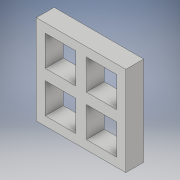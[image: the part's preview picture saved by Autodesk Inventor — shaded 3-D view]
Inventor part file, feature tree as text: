
AUTODESK INVENTOR PART (.ipt)
format: ipt  version: 2018 (Build 220112000, 112)  size: 120,320 bytes
history: native  units: mm
features: extrude x1, sketch x1
ambient origin geometry x8: Origin, YZ Plane, XZ Plane, XY Plane, X Axis, Y Axis, Z Axis, Center Point
bodies: Volumenkörper1 (feature_tree)
feature tree (2):
  extrude  "Extrusion1"  Depth=25.0mm
  sketch  "Skizze1"  dims[d0=25.0mm d1=25.0mm d2=8.5mm d3=8.5mm d4=8.5mm d5=8.5mm d6=8.5mm d7=8.5mm d8=8.5mm d9=8.5mm d10=2.5mm d11=2.5mm d12=2.5mm d13=5.0mm d14=0.0mm]
